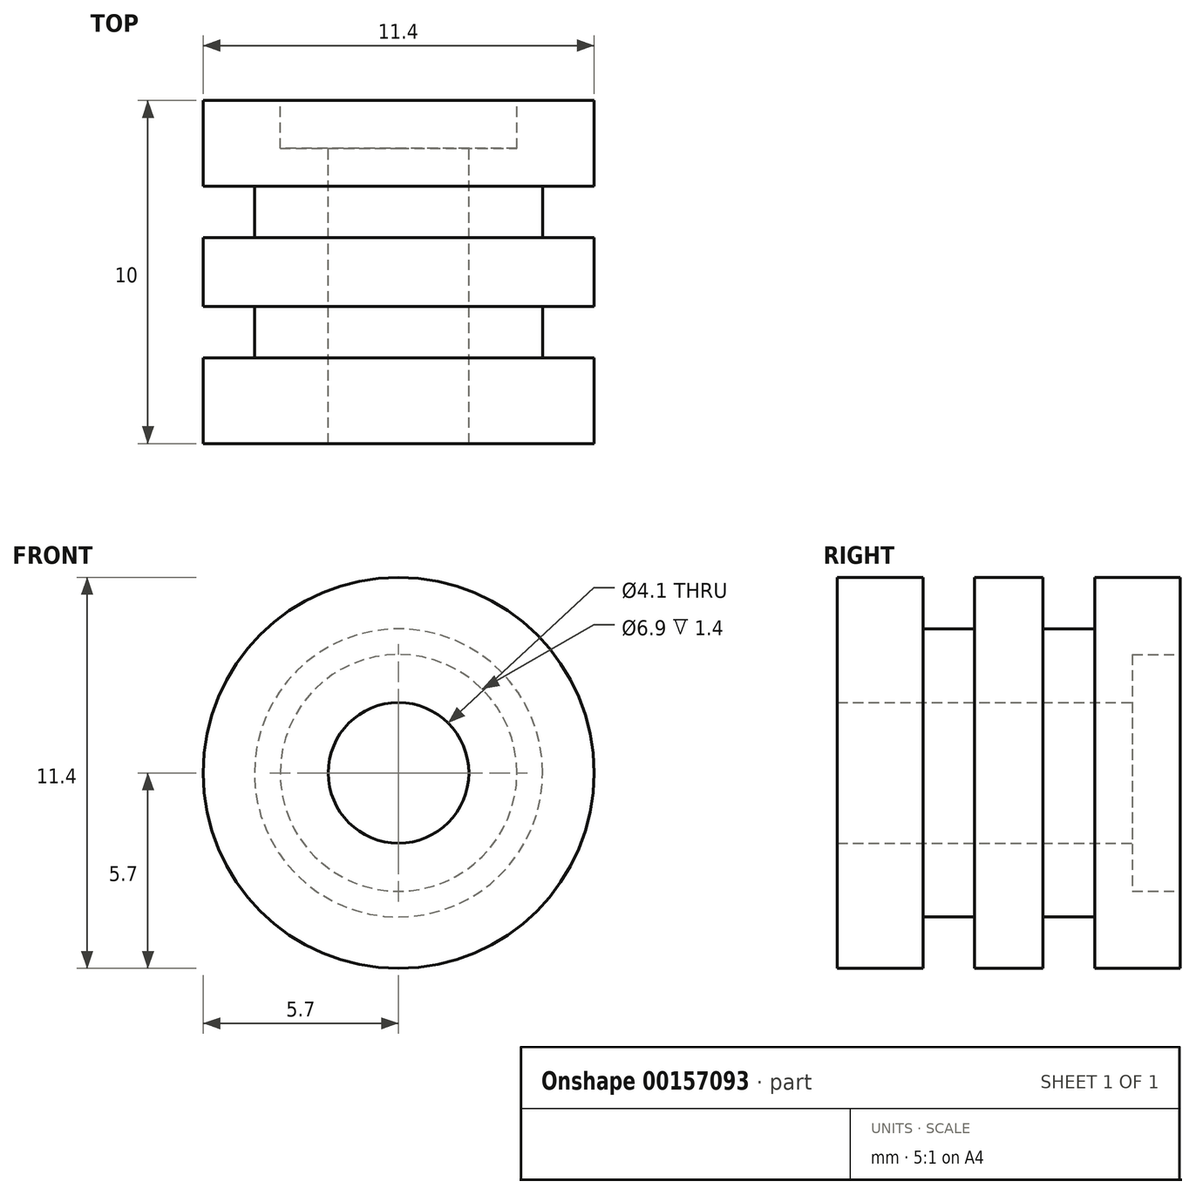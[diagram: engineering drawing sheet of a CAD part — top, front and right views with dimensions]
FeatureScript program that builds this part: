
annotation { "Feature Type Name" : "Feature", "Feature Type Description" : "" }
export const myFeature = defineFeature(function(context is Context, id is Id, definition is map)
    precondition{}
    {
        {
            var Q0;
            Q0=qCreatedBy(makeId("Right.planeOp"),FACE);
            var sketch = newSketch(context, id + "F0", { "sketchPlane" : qUnion([Q0])});
            skLineSegment(sketch, "E0", {"start": v(11.47, 0) * mm, "end": v(0, 0) * mm, "construction": true});
            skLineSegment(sketch, "E1", {"start": v(8.6, 2.05) * mm, "end": v(0, 2.05) * mm});
            skLineSegment(sketch, "E2", {"start": v(8.6, 2.05) * mm, "end": v(8.6, 3.45) * mm});
            skLineSegment(sketch, "E3", {"start": v(10, 3.45) * mm, "end": v(8.6, 3.45) * mm});
            skLineSegment(sketch, "E4", {"start": v(10, 3.45) * mm, "end": v(10, 5.7) * mm});
            skLineSegment(sketch, "E5", {"start": v(7.5, 5.7) * mm, "end": v(10, 5.7) * mm});
            skLineSegment(sketch, "E6", {"start": v(7.5, 5.7) * mm, "end": v(7.5, 4.2) * mm});
            skLineSegment(sketch, "E7", {"start": v(6, 4.2) * mm, "end": v(7.5, 4.2) * mm});
            skLineSegment(sketch, "E8", {"start": v(2.5, 4.2) * mm, "end": v(2.5, 5.7) * mm});
            skLineSegment(sketch, "E9", {"start": v(0, 5.7) * mm, "end": v(2.5, 5.7) * mm});
            skLineSegment(sketch, "E10", {"start": v(0, 5.7) * mm, "end": v(0, 2.05) * mm});
            skLineSegment(sketch, "E11", {"start": v(4, 4.2) * mm, "end": v(4, 5.7) * mm});
            skLineSegment(sketch, "E12", {"start": v(4, 5.7) * mm, "end": v(6, 5.7) * mm});
            skLineSegment(sketch, "E13", {"start": v(6, 5.7) * mm, "end": v(6, 4.2) * mm});
            skLineSegment(sketch, "E14.trimOffspring", {"start": v(4, 4.2) * mm, "end": v(2.5, 4.2) * mm});
            skSolve(sketch);
        }
        {
            var Q0;
            Q0=makeQuery(id+"F0.imprint","IMPRINT",FACE,{"disambiguationData":[TD([[makeQuery(id+"F0.imprint","IMPRINT",EDGE,{"derivedFrom":sQuery(id+"F0.wireOp",EDGE,"E1")}),-1.0]])]});
            var Q1;
            Q1=sQuery(id+"F0.wireOp",EDGE,"E0");
            revolve(context, id + "F1", {"entities" : qUnion([Q0]), "axis" : qUnion([Q1]), "revolveType" : RevolveType.FULL});
        }
    });
